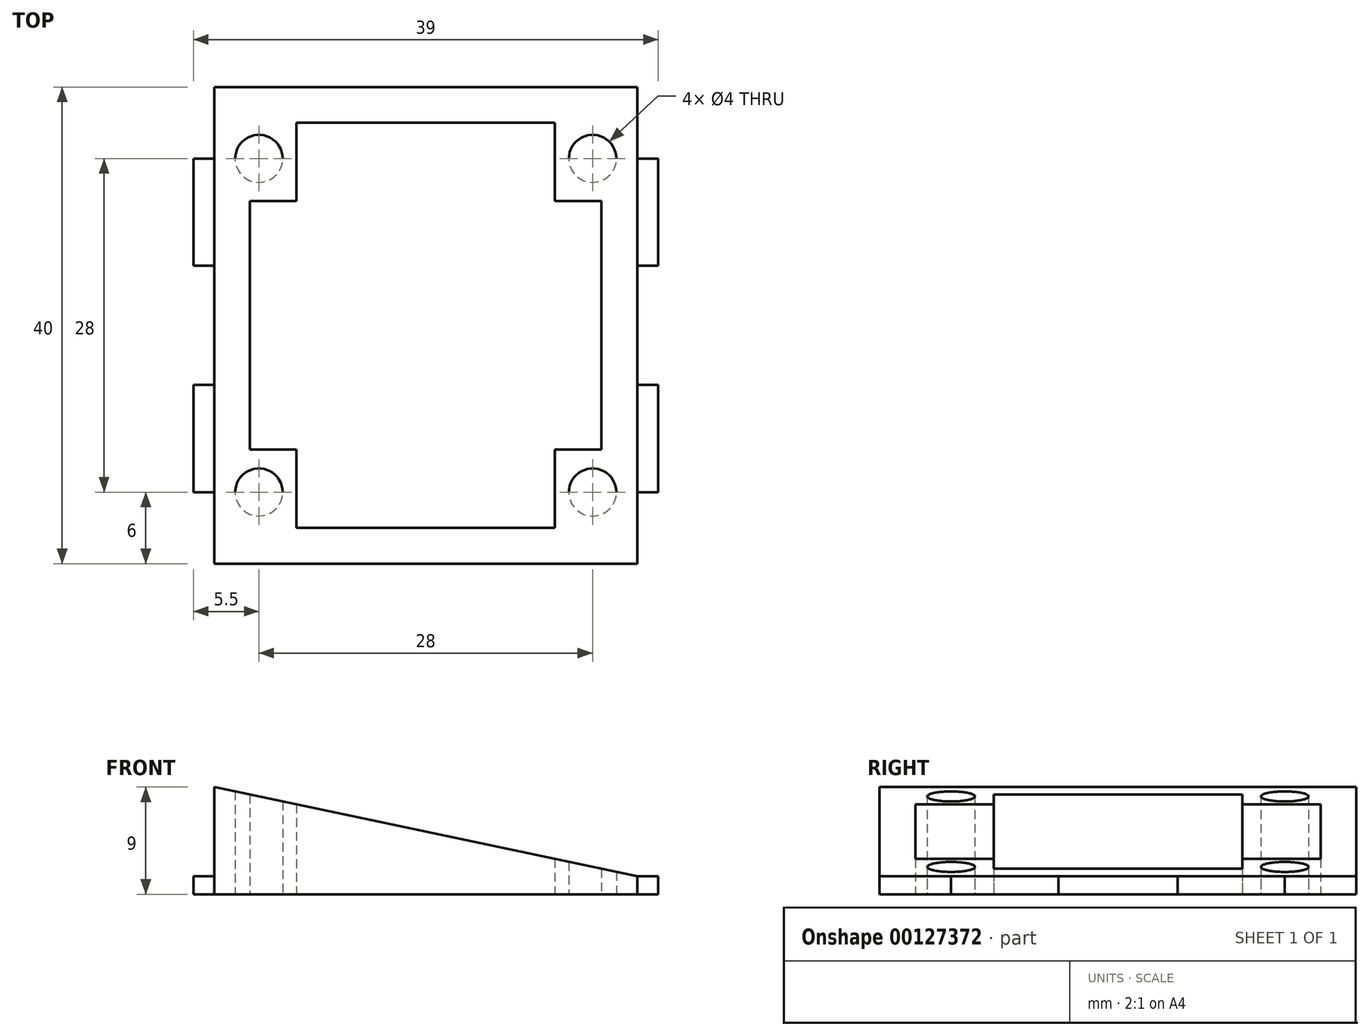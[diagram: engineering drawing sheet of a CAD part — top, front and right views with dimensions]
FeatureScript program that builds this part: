
annotation { "Feature Type Name" : "Feature", "Feature Type Description" : "" }
export const myFeature = defineFeature(function(context is Context, id is Id, definition is map)
    precondition{}
    {
        {
            var Q0;
            Q0=qCreatedBy(makeId("Front.planeOp"),FACE);
            var sketch = newSketch(context, id + "F0", { "sketchPlane" : qUnion([Q0])});
            skLineSegment(sketch, "E0", {"start": v(0, 0) * mm, "end": v(0, 9) * mm});
            skLineSegment(sketch, "E1", {"start": v(0, 9) * mm, "end": v(35.5, 1.5) * mm});
            skLineSegment(sketch, "E2", {"start": v(35.5, 1.5) * mm, "end": v(35.5, 0) * mm});
            skLineSegment(sketch, "E3", {"start": v(35.5, 0) * mm, "end": v(0, 0) * mm});
            skSolve(sketch);
        }
        {
            var Q0;
            Q0 = qSketchRegion(id + "F0", true);
            extrude(context, id + "F1", {"entities" : qUnion([Q0]), "depth" : 40 * mm});
        }
        {
            var Q0;
            Q0=makeQuery(id+"F1.opExtrude","SWEPT_FACE",FACE,{"disambiguationData":[OSD([sQuery(id+"F0.wireOp",EDGE,"E3")])]});
            var sketch = newSketch(context, id + "F2", { "sketchPlane" : qUnion([Q0])});
            skLineSegment(sketch, "E4.bottom", {"start": v(3.75, 6) * mm, "end": v(31.75, 6) * mm});
            skLineSegment(sketch, "E4.top", {"start": v(3.75, 34) * mm, "end": v(31.75, 34) * mm});
            skLineSegment(sketch, "E4.left", {"start": v(3.75, 6) * mm, "end": v(3.75, 34) * mm});
            skLineSegment(sketch, "E4.right", {"start": v(31.75, 6) * mm, "end": v(31.75, 34) * mm});
            skLineSegment(sketch, "E5", {"start": v(3.75, 34) * mm, "end": v(3.75, 40) * mm});
            skLineSegment(sketch, "E6", {"start": v(3.75, 6) * mm, "end": v(3.75, 0) * mm});
            skLineSegment(sketch, "E7", {"start": v(3.75, 34) * mm, "end": v(0, 34) * mm});
            skLineSegment(sketch, "E8", {"start": v(31.75, 34) * mm, "end": v(35.5, 34) * mm});
            skSolve(sketch);
        }
        {
            var Q0;
            Q0=sQuery(id+"F2.wireOp",VERTEX,"E4.left.end");
            var Q1;
            Q1=sQuery(id+"F2.wireOp",VERTEX,"E4.top.end");
            var Q2;
            Q2=sQuery(id+"F2.wireOp",VERTEX,"E4.right.start");
            var Q3;
            Q3=sQuery(id+"F2.wireOp",VERTEX,"E4.left.start");
            var Q4;
            Q4=makeQuery(id+"F1.opExtrude","SWEPT_BODY",BODY,{"disambiguationData":[OSD([sQuery(id+"F0.wireOp",EDGE,"E0"),sQuery(id+"F0.wireOp",EDGE,"E1"),sQuery(id+"F0.wireOp",EDGE,"E2"),sQuery(id+"F0.wireOp",EDGE,"E3")])]});
            hole(context, id + "F3", {"style" : HoleStyle.SIMPLE, "endStyle" : HoleEndStyle.THROUGH, "holeDiameter" : 4 * mm, "locations" : qUnion([Q0, Q1, Q2, Q3]), "scope" : qUnion([Q4]), "isTappedThrough" : true});
        }
        {
            var Q0;
            Q0=makeQuery(id+"F1.opExtrude","SWEPT_FACE",FACE,{"disambiguationData":[OSD([sQuery(id+"F0.wireOp",EDGE,"E0")])]});
            var sketch = newSketch(context, id + "F4", { "sketchPlane" : qUnion([Q0])});
            skLineSegment(sketch, "E9.bottom", {"start": v(6, 1.5) * mm, "end": v(15, 1.5) * mm});
            skLineSegment(sketch, "E9.top", {"start": v(6, 0) * mm, "end": v(15, 0) * mm});
            skLineSegment(sketch, "E9.left", {"start": v(6, 1.5) * mm, "end": v(6, 0) * mm});
            skLineSegment(sketch, "E9.right", {"start": v(15, 1.5) * mm, "end": v(15, 0) * mm});
            skLineSegment(sketch, "E10.bottom", {"start": v(25, 1.5) * mm, "end": v(34, 1.5) * mm});
            skLineSegment(sketch, "E10.top", {"start": v(25, 0) * mm, "end": v(34, 0) * mm});
            skLineSegment(sketch, "E10.left", {"start": v(25, 1.5) * mm, "end": v(25, 0) * mm});
            skLineSegment(sketch, "E10.right", {"start": v(34, 1.5) * mm, "end": v(34, 0) * mm});
            skLineSegment(sketch, "E11", {"start": v(15, 0) * mm, "end": v(25, 0) * mm});
            skLineSegment(sketch, "E12", {"start": v(34, 0) * mm, "end": v(40, 0) * mm});
            skLineSegment(sketch, "E13", {"start": v(0, 0) * mm, "end": v(6, 0) * mm});
            skSolve(sketch);
        }
        {
            var Q0;
            Q0 = qSketchRegion(id + "F4", true);
            extrude(context, id + "F5", {"entities" : qUnion([Q0]), "operationType" : NewBodyOperationType.ADD, "depth" : 1.75 * mm});
        }
        {
            var Q0;
            Q0=makeQuery(id+"F1.opExtrude","SWEPT_FACE",FACE,{"disambiguationData":[OSD([sQuery(id+"F0.wireOp",EDGE,"E2")])]});
            var sketch = newSketch(context, id + "F6", { "sketchPlane" : qUnion([Q0])});
            skLineSegment(sketch, "E14.bottom", {"start": v(-34, 1.5) * mm, "end": v(-25, 1.5) * mm});
            skLineSegment(sketch, "E14.top", {"start": v(-34, 0) * mm, "end": v(-25, 0) * mm});
            skLineSegment(sketch, "E14.left", {"start": v(-34, 1.5) * mm, "end": v(-34, 0) * mm});
            skLineSegment(sketch, "E14.right", {"start": v(-25, 1.5) * mm, "end": v(-25, 0) * mm});
            skLineSegment(sketch, "E15.bottom", {"start": v(-15, 1.5) * mm, "end": v(-6, 1.5) * mm});
            skLineSegment(sketch, "E15.top", {"start": v(-15, 0) * mm, "end": v(-6, 0) * mm});
            skLineSegment(sketch, "E15.left", {"start": v(-15, 1.5) * mm, "end": v(-15, 0) * mm});
            skLineSegment(sketch, "E15.right", {"start": v(-6, 1.5) * mm, "end": v(-6, 0) * mm});
            skLineSegment(sketch, "E16", {"start": v(-25, 0) * mm, "end": v(-15, 0) * mm});
            skLineSegment(sketch, "E17", {"start": v(-6, 0) * mm, "end": v(0, 0) * mm});
            skLineSegment(sketch, "E18", {"start": v(-40, 0) * mm, "end": v(-34, 0) * mm});
            skSolve(sketch);
        }
        {
            var Q0;
            Q0 = qSketchRegion(id + "F6", true);
            extrude(context, id + "F7", {"entities" : qUnion([Q0]), "operationType" : NewBodyOperationType.ADD, "depth" : 1.75 * mm});
        }
        {
            var Q0;
            Q0=makeQuery(id+"F7.boolean.opBoolean","MERGE",FACE,{"derivedFrom":[makeQuery(id+"F5.boolean.opBoolean","MERGE",FACE,{"derivedFrom":[makeQuery(id+"F1.opExtrude","SWEPT_FACE",FACE,{"disambiguationData":[OSD([sQuery(id+"F0.wireOp",EDGE,"E3")])]}),makeQuery(id+"F5.opExtrude","SWEPT_FACE",FACE,{"disambiguationData":[OSD([sQuery(id+"F4.wireOp",EDGE,"E9.top")])]}),makeQuery(id+"F5.opExtrude","SWEPT_FACE",FACE,{"disambiguationData":[OSD([sQuery(id+"F4.wireOp",EDGE,"E10.top")])]})]}),makeQuery(id+"F7.opExtrude","SWEPT_FACE",FACE,{"disambiguationData":[OSD([sQuery(id+"F6.wireOp",EDGE,"E14.top")])]}),makeQuery(id+"F7.opExtrude","SWEPT_FACE",FACE,{"disambiguationData":[OSD([sQuery(id+"F6.wireOp",EDGE,"E15.top")])]})]});
            var sketch = newSketch(context, id + "F8", { "sketchPlane" : qUnion([Q0])});
            skLineSegment(sketch, "E19", {"start": v(17.75, 20) * mm, "end": v(35.5, 20) * mm});
            skPoint(sketch, "E19.endSnap0", {"position": v(35.5, 20) * mm});
            skLineSegment(sketch, "E20", {"start": v(17.75, 20) * mm, "end": v(0, 20) * mm});
            skPoint(sketch, "E20.endSnap0", {"position": v(0, 20) * mm});
            skLineSegment(sketch, "E21", {"start": v(17.75, 20) * mm, "end": v(17.75, 40) * mm});
            skLineSegment(sketch, "E22", {"start": v(17.75, 20) * mm, "end": v(17.75, 0) * mm});
            skLineSegment(sketch, "E23.bottom", {"start": v(6.9, 37) * mm, "end": v(28.6, 37) * mm});
            skLineSegment(sketch, "E23.top", {"start": v(6.9, 3) * mm, "end": v(28.6, 3) * mm});
            skLineSegment(sketch, "E23.left", {"start": v(6.9, 37) * mm, "end": v(6.9, 3) * mm});
            skLineSegment(sketch, "E23.right", {"start": v(28.6, 37) * mm, "end": v(28.6, 3) * mm});
            skPoint(sketch, "E23.middle", {"position": v(17.75, 20) * mm});
            skLineSegment(sketch, "E24.bottom", {"start": v(3, 30.43) * mm, "end": v(32.5, 30.43) * mm});
            skLineSegment(sketch, "E24.top", {"start": v(3, 9.57) * mm, "end": v(32.5, 9.57) * mm});
            skLineSegment(sketch, "E24.left", {"start": v(3, 30.43) * mm, "end": v(3, 9.57) * mm});
            skLineSegment(sketch, "E24.right", {"start": v(32.5, 30.43) * mm, "end": v(32.5, 9.57) * mm});
            skSolve(sketch);
        }
        {
            var Q0;
            Q0 = qSketchRegion(id + "F8", true);
            extrude(context, id + "F9", {"entities" : qUnion([Q0]), "operationType" : NewBodyOperationType.REMOVE, "endBound" : BoundingType.THROUGH_ALL, "oppositeDirection" : true, "depth" : 25 * mm});
        }
    });
